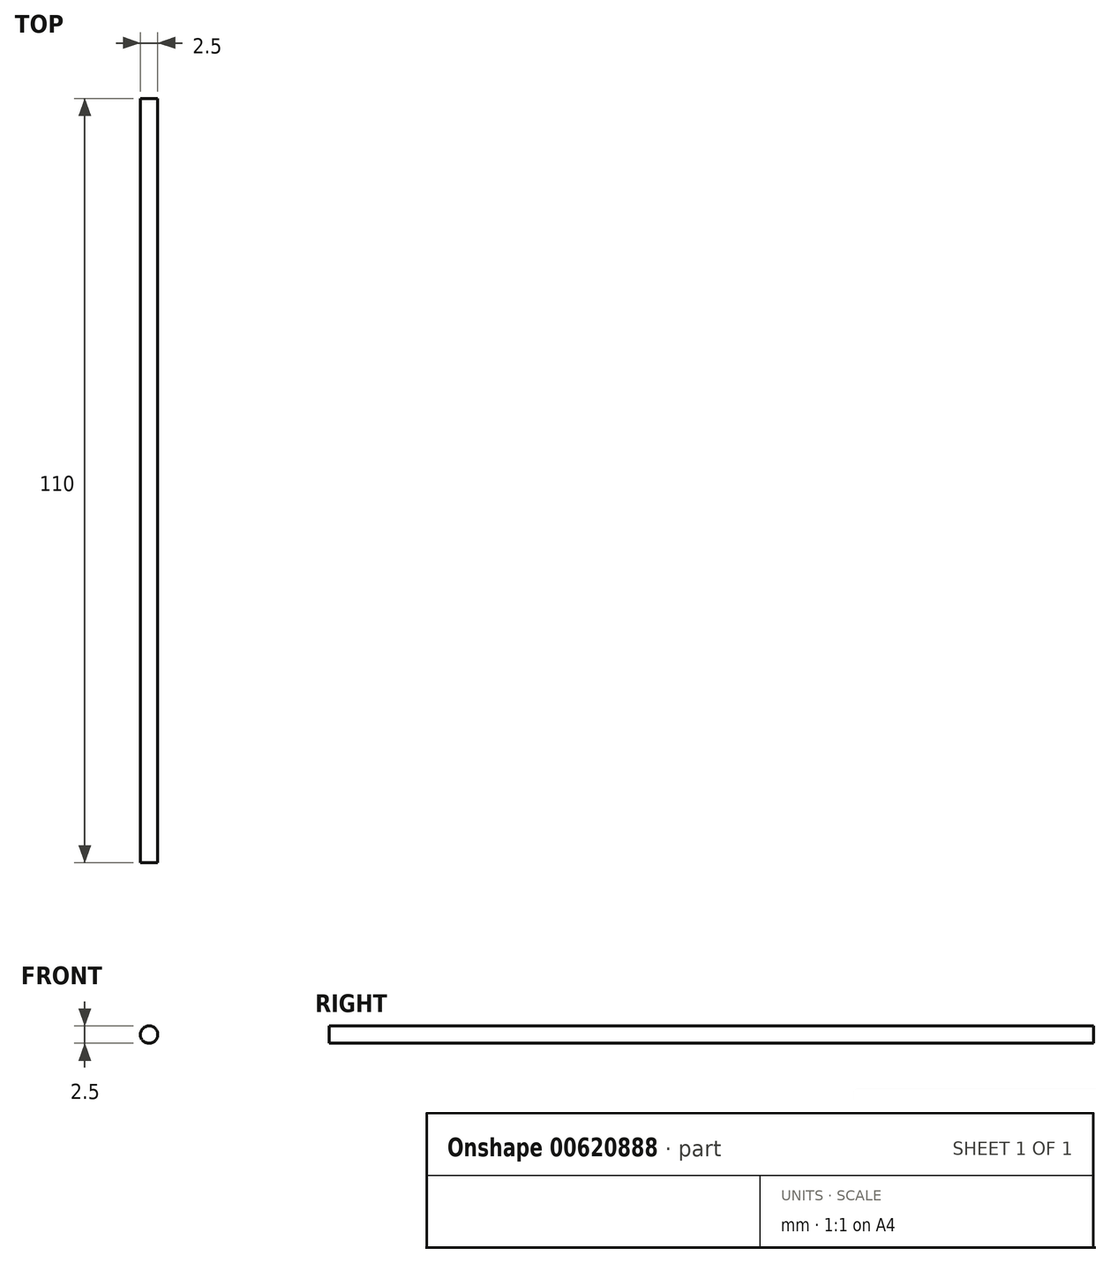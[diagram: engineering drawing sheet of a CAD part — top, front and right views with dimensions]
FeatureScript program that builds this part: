
annotation { "Feature Type Name" : "Feature", "Feature Type Description" : "" }
export const myFeature = defineFeature(function(context is Context, id is Id, definition is map)
    precondition{}
    {
        {
            var Q0;
            Q0=qCreatedBy(makeId("Front.planeOp"),FACE);
            var sketch = newSketch(context, id + "F0", { "sketchPlane" : qUnion([Q0])});
            skCircle(sketch, "E0", {"center": v(0, 0) * mm, "radius": 1.25 * mm});
            skSolve(sketch);
        }
        {
            var Q0;
            Q0=makeQuery(id+"F0.imprint","IMPRINT",FACE,{"disambiguationData":[TD([[makeQuery(id+"F0.imprint","IMPRINT",EDGE,{"derivedFrom":sQuery(id+"F0.wireOp",EDGE,"E0")}),1.0]])]});
            extrude(context, id + "F1", {"entities" : qUnion([Q0]), "depth" : 110 * mm, "offsetDistance" : 25 * mm});
        }
    });
